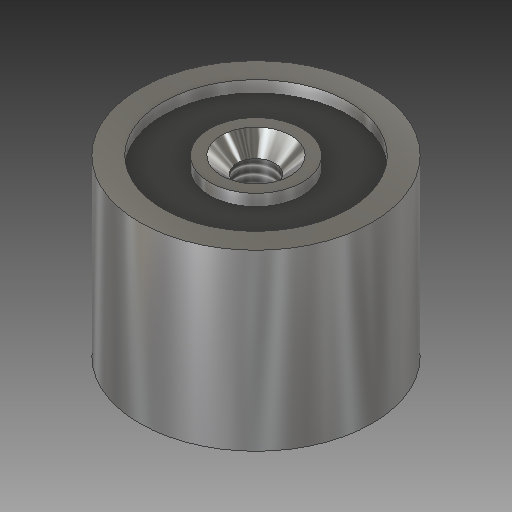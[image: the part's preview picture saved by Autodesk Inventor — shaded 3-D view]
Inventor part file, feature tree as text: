
AUTODESK INVENTOR PART (.ipt)
format: ipt  version: 2019 (Build 230136000, 136)  size: 171,008 bytes
history: native  units: mm
features: sketch x4, other x3
ambient origin geometry x8: Origin, YZ Plane, XZ Plane, XY Plane, X Axis, Y Axis, Z Axis, Center Point
bodies: Solid1 (feature_tree)
feature tree (7):
  other  "20-15 Electromagnet.ipt"
  other  "Solid1::20-15 Electromagnet.ipt"
  other  "TaggingFeature1"
  sketch  "Sketch1"  dims[d0=10.0mm]
  sketch  "Sketch2"
  sketch  "Sketch3"
  sketch  "Sketch5"
